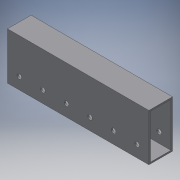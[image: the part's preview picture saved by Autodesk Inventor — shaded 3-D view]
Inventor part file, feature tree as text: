
AUTODESK INVENTOR PART (.ipt)
format: ipt  version: 2018 (Build 220112000, 112)  size: 132,608 bytes
history: native  units: in
note: dims shown in document units (in); Inventor stores cm internally (conversion verified against a paired STEP export)
features: extrude x2, sketch x2
ambient origin geometry x8: Origin, YZ Plane, XZ Plane, XY Plane, X Axis, Y Axis, Z Axis, Center Point
bodies: Solid1 (feature_tree)
feature tree (4):
  extrude  "Extrusion1"  Depth=2.0in
  extrude  "Extrusion2"  Depth=0.065in
  sketch  "Sketch1"  dims[d0=1.0in d1=2.0in]
  sketch  "Sketch2"  dims[d2=0.065in d3=0.065in d4=0.065in d5=0.065in d6=6.0in d7=0.0in d8=0.2031in d9=0.2031in d13=0.2031in d14=0.2031in d15=0.2031in d16=0.2031in d17=1.0in d18=0.5in d20=3.5in d21=0.5in d22=0.5in d23=2.5in d24=1.0in d25=0.5in d26=0.5in d27=0.5in d28=0.5in d29=0.5in d30=1.0in d31=0.0in]
